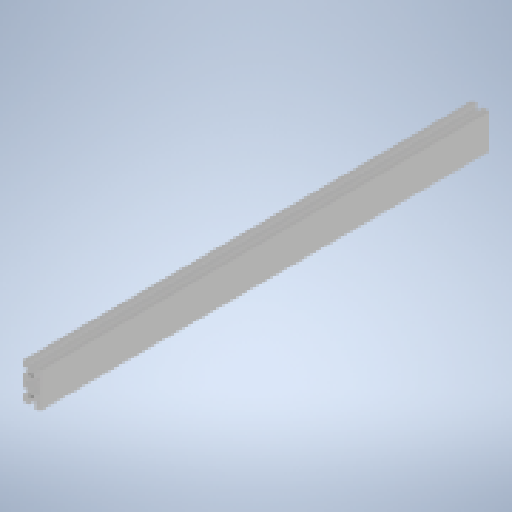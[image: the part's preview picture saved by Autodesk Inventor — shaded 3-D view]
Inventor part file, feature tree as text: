
AUTODESK INVENTOR PART (.ipt)
format: ipt  version: 2024 (Build 280153000, 153)  size: 387,072 bytes
history: native  units: mm
features: other x7, thread x4, sketch x2, extrude x1, hole x1, pattern_linear x1
ambient origin geometry x8: Origin, YZ Plane, XZ Plane, XY Plane, X Axis, Y Axis, Z Axis, Center Point
bodies: Solid1 (feature_tree)
feature tree (16):
  extrude  "Extrusion1"  Depth=20.0mm TaperAngle=0.0deg
  hole  "Hole1"  [1 undecoded]
  pattern_linear  "Rectangular Pattern1"  Spacing1=10.0mm  [1 undecoded]
  other  "C1_XY"
  other  "C1_YZ"
  other  "C1_ZX"
  other  "C1_X"
  other  "C1_Y"
  other  "C1_Z"
  other  "C1_Center"
  thread  "Thread1"  [1 undecoded]
  thread  "Thread2"  [1 undecoded]
  thread  "Thread3"  [1 undecoded]
  thread  "Thread4"  [1 undecoded]
  sketch  "Sketch_63"  dims[d2=4.2mm d3=6.0mm d4=4.0mm d5=2.0mm d6=90.0deg d7=425.0mm d8=0.0mm d9=20.0mm d11=20.0mm d12=10.0mm d14=0.0mm d15=0.0mm d16=10.0mm d17=0.0mm d18=10.0mm d19=0.0mm d20=10.0mm d21=0.0mm d22=10.0mm d23=0.0mm]
  sketch  "Sketch2"  dims[d0=500.0mm d1=0.0mm]
note: 6 required parameter values undecoded (feature->parameter linkage not recoverable at this tier; creation-order binding heuristic only, values carry confidence <= 0.55)
